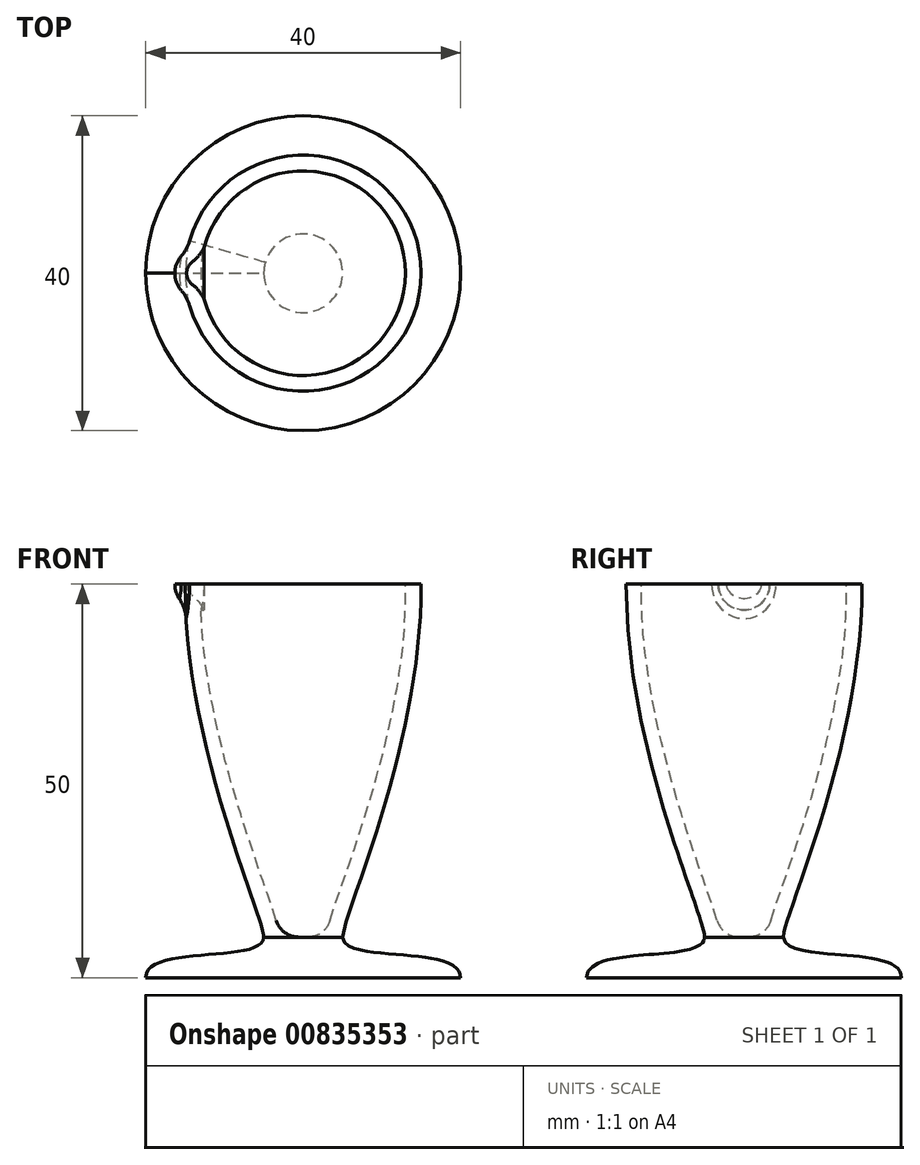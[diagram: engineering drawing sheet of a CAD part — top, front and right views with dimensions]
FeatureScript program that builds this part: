
annotation { "Feature Type Name" : "Feature", "Feature Type Description" : "" }
export const myFeature = defineFeature(function(context is Context, id is Id, definition is map)
    precondition{}
    {
        {
            var Q0;
            Q0=qCreatedBy(makeId("Right.planeOp"),FACE);
            var sketch = newSketch(context, id + "F0", { "sketchPlane" : qUnion([Q0])});
            skLineSegment(sketch, "E0", {"start": v(0, 0) * mm, "end": v(20, 0) * mm});
            skLineSegment(sketch, "E1", {"start": v(0, 0) * mm, "end": v(0, 50) * mm});
            skFitSpline(sketch, "E2", {"points": [v(20, 0) * mm, v(5, 5.16) * mm], "startDerivative": vector(0, 13.01) * mm, "endDerivative": vector(0, 10.42) * mm});
            skFitSpline(sketch, "E3", {"points": [v(5, 5.16) * mm, v(15, 50) * mm], "startDerivative": vector(0, 8.43) * mm, "endDerivative": vector(0, 63.1) * mm});
            skFitSpline(sketch, "E4.0", {"points": [v(3, 5.16) * mm, v(3, 5.27) * mm, v(3.01, 5.49) * mm, v(3.06, 5.88) * mm, v(3.16, 6.34) * mm, v(3.31, 6.94) * mm, v(3.58, 7.83) * mm, v(4, 9.13) * mm, v(4.66, 11) * mm, v(5.42, 13.17) * mm, v(6.26, 15.63) * mm, v(7.16, 18.35) * mm, v(8.4, 22.27) * mm, v(9.94, 27.7) * mm, v(11.55, 34.82) * mm, v(12.7, 42.33) * mm, v(13, 47.45) * mm, v(13, 50) * mm]});
            skLineSegment(sketch, "E5", {"start": v(15, 50) * mm, "end": v(13, 50) * mm});
            skLineSegment(sketch, "E6", {"start": v(3, 5.16) * mm, "end": v(0, 5.16) * mm});
            skSolve(sketch);
        }
        {
            var Q0;
            {var subQ1=sQuery(id+"F0.wireOp",EDGE,"E0");Q0=makeQuery(id+"F0.imprint","IMPRINT",FACE,{"disambiguationData":[TD([[makeQuery(id+"F0.imprint","IMPRINT",EDGE,{"derivedFrom":subQ1}),1.0]])]});}
            var Q1;
            Q1=sQuery(id+"F0.wireOp",EDGE,"E1");
            revolve(context, id + "F1", {"surfaceOperationType" : NewSurfaceOperationType.NEW, "entities" : qUnion([Q0]), "axis" : qUnion([Q1]), "revolveType" : RevolveType.FULL});
        }
        {
            var Q0;
            Q0=makeQuery(id+"F1.opRevolve","SWEPT_EDGE",EDGE,{"disambiguationData":[OSD([sQuery(id+"F0.wireOp",EDGE,"E4.0"),sQuery(id+"F0.wireOp",EDGE,"E6")])]});
            fillet(context, id + "F2", {"entities" : qUnion([Q0]), "radius" : 3 * mm, "tangentPropagation" : true, "allowEdgeOverflow" : false});
        }
        {
            var Q0;
            Q0=makeQuery(id+"F1.opRevolve","SWEPT_FACE",FACE,{"disambiguationData":[OSD([sQuery(id+"F0.wireOp",EDGE,"E5")])]});
            var sketch = newSketch(context, id + "F3", { "sketchPlane" : qUnion([Q0])});
            skLineSegment(sketch, "E7", {"start": v(-15, 0) * mm, "end": v(-13, 0) * mm});
            skCircle(sketch, "E8", {"center": v(-13, 0) * mm, "radius": 1.8 * mm});
            skLineSegment(sketch, "E9", {"start": v(-15, 0) * mm, "end": v(-16.3, 0) * mm});
            skArc(sketch, "E10", {"start": v(-16.3, 0) * mm, "mid": v(-15.18, 2.48) * mm, "end": v(-12.58, 3.27) * mm});
            skSolve(sketch);
        }
        {
            var Q0;
            {var subQ0=sQuery(id+"F3.wireOp",EDGE,"E9");Q0=makeQuery(id+"F3.imprint","IMPRINT",FACE,{"disambiguationData":[TD([[makeQuery(id+"F3.imprint","IMPRINT",EDGE,{"derivedFrom":subQ0}),-1.0]])]});}
            var Q1;
            {var subQ0=sQuery(id+"F3.wireOp",EDGE,"E7");var subQ8=sQuery(id+"F3.wireOp",EDGE,"E8");var subQ9=makeQuery(id+"F3.imprint","INTERSECT",VERTEX,{"derivedFrom":[subQ0,subQ8]});Q1=makeQuery(id+"F3.imprint","IMPRINT",FACE,{"disambiguationData":[TD([[makeQuery(id+"F3.imprint","IMPRINT",EDGE,{"disambiguationData":[TD([[subQ9,1.0]])],"derivedFrom":subQ8}),-1.0]])]});}
            var Q2;
            Q2=sQuery(id+"F3.wireOp",EDGE,"E8");
            var Q3;
            Q3=sQuery(id+"F3.wireOp",EDGE,"E7");
            revolve(context, id + "F4", {"operationType" : NewBodyOperationType.ADD, "surfaceOperationType" : NewSurfaceOperationType.NEW, "entities" : qUnion([Q0, Q1]), "surfaceEntities" : qUnion([Q2]), "axis" : qUnion([Q3]), "revolveType" : RevolveType.ONE_DIRECTION, "oppositeDirection" : true, "angle" : 180 * degree});
        }
        {
            var Q0;
            {var subQ0=sQuery(id+"F3.wireOp",EDGE,"E7");var subQ3=sQuery(id+"F3.wireOp",EDGE,"E8");var subQ4=makeQuery(id+"F3.imprint","INTERSECT",VERTEX,{"derivedFrom":[subQ0,subQ3]});Q0=makeQuery(id+"F3.imprint","IMPRINT",FACE,{"disambiguationData":[TD([[makeQuery(id+"F3.imprint","IMPRINT",EDGE,{"disambiguationData":[TD([[subQ4,-1.0]])],"derivedFrom":subQ0}),-1.0]])]});}
            var Q1;
            Q1=sQuery(id+"F3.wireOp",EDGE,"E7");
            revolve(context, id + "F5", {"operationType" : NewBodyOperationType.REMOVE, "surfaceOperationType" : NewSurfaceOperationType.NEW, "entities" : qUnion([Q0]), "axis" : qUnion([Q1]), "revolveType" : RevolveType.FULL, "oppositeDirection" : true});
        }
        {
            var Q0;
            Q0=makeQuery(id+"F4.opRevolve","SWEPT_EDGE",EDGE,{"disambiguationData":[OSD([sQuery(id+"F0.wireOp",EDGE,"E4.0"),sQuery(id+"F0.wireOp",EDGE,"E5"),sQuery(id+"F3.wireOp",EDGE,"E8")])]});
            var Q1;
            Q1=makeQuery(id+"F4.boolean.opBoolean","INTERSECT",EDGE,{"derivedFrom":[makeQuery(id+"F1.opRevolve","SWEPT_FACE",FACE,{"disambiguationData":[OSD([sQuery(id+"F0.wireOp",EDGE,"E3")])]}),makeQuery(id+"F4.opRevolve","SWEPT_FACE",FACE,{"disambiguationData":[OSD([sQuery(id+"F3.wireOp",EDGE,"E10")])]})]});
            fillet(context, id + "F6", {"entities" : qUnion([Q0, Q1]), "radius" : 5 * mm, "tangentPropagation" : true, "allowEdgeOverflow" : false});
        }
    });
